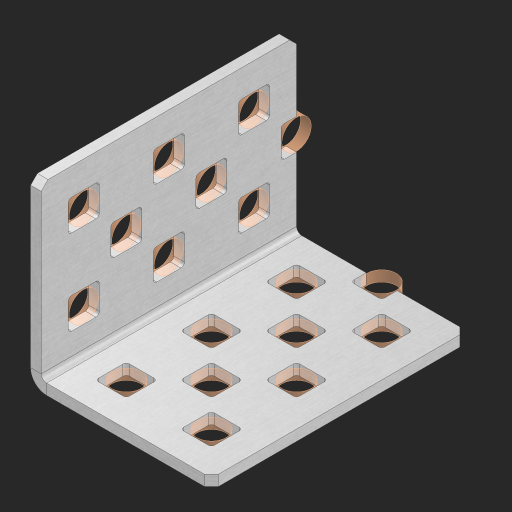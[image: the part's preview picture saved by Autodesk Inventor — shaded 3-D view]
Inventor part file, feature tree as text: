
AUTODESK INVENTOR PART (.ipt)
format: ipt  version: 2023 (Build 270158000, 158)  size: 625,152 bytes
history: native  units: in
note: dims shown in document units (in); Inventor stores cm internally (conversion verified against a paired STEP export)
features: other x24, extrude x16, sheet_metal_op x8, sketch x7, pattern_linear x2, mirror x1, chamfer x1
ambient origin geometry x8: Origin, YZ Plane, XZ Plane, XY Plane, X Axis, Y Axis, Z Axis, Center Point
bodies: Solid1 (feature_tree), Body (feature_tree)
feature tree (59):
  sheet_metal_op  "Flanges"
  sheet_metal_op  "Body Pattern"
  pattern_linear  "Center Pattern"  Spacing1=1.0in  [1 undecoded]
  other  "Arc Length"
  pattern_linear  "Notch Pattern"  Spacing1=0.25in  [1 undecoded]
  other  "Diagonal Plane"
  mirror  "Everything Mirrored"
  chamfer  "End Chamfer"
  sketch  "Sketch1"  dims[d0=1.0in]
  other  "Plate1"
  sketch  "Sketch2"  dims[d1=1.5in]
  other  "Plate2"
  sheet_metal_op  "Bend1"
  sheet_metal_op  "Corner1"
  sketch  "Sketch8"  dims[d2=0.0625in]
  sketch  "Sketch9"  dims[d3=0.0625in]
  other  "Srf91"
  sheet_metal_op  "Body Pattern Sketch"
  other  "Srf92"
  sketch  "Sketch13"  dims[d4=0.0312in]
  sketch  "Sketch15"  dims[d5=0.125in]
  sketch  "Sketch16"  dims[d6=0.0625in d7=1.0in d8=90.0deg d9=0.0312in d10=0.25in d11=0.0625in d12=0.0625in d49=0.182in d50=0.02in d52=0.25in d53=0.0625in d54=0.0in d55=0.172in d56=1.0in d57=0.0in d60=1.1811in d62=0.5in d63=0.7874in d65=0.5in d85=0.1473in d86=0.1782in d89=0.0625in d90=0.0in d91=0.04in d92=0.0491in d95=2.5in d96=0.04in d97=0.25in d98=45.0deg d99=0.25in d106=0.182in d107=0.02in d108=0.5in d110=0.0625in d111=0.0in d112=0.172in d113=0.5in d114=0.0in d117=0.5in d123=0.25in d125=0.25in d126=0.0491in d127=0.1473in d128=0.08in d129=0.04in d130=2.5in]
  other  "Srf786"
  other  "Srf856"
  other  "Srf857"
  other  "Srf858"
  other  "Srf859"
  other  "Srf889"
  other  "Srf890"
  other  "Srf1275"
  other  "Srf1276"
  other  "Srf1278"
  other  "Srf1279"
  other  "Srf1280"
  other  "Srf1281"
  other  "Srf1277"
  other  "Srf1285"
  other  "Srf1286"
  sheet_metal_op  "Body Stamp"
  sheet_metal_op  "Body Circle"
  other  "Center Stamp"
  other  "Center Circle"
  sheet_metal_op  "Notch"
  extrude  "ExtrusionSrf92"  Depth=0.0625in
  extrude  "ExtrusionSrf856"  Depth=0.0625in
  extrude  "ExtrusionSrf857"  Depth=0.182in
  extrude  "ExtrusionSrf858"  Depth=0.02in
  extrude  "ExtrusionSrf859"  Depth=0.25in
  extrude  "ExtrusionSrf889"  Depth=0.0625in
  extrude  "ExtrusionSrf890"  TaperAngle=0.0deg  [1 undecoded]
  extrude  "ExtrusionSrf1275"  Depth=0.25in
  extrude  "ExtrusionSrf1276"  Depth=1.0in TaperAngle=0.0deg
  extrude  "ExtrusionSrf1277"  Depth=0.25in
  extrude  "ExtrusionSrf1278"  Depth=0.5in
  extrude  "ExtrusionSrf1279"  Depth=0.25in
  extrude  "ExtrusionSrf1280"  Depth=0.25in
  extrude  "ExtrusionSrf1345"  Depth=0.0625in
  extrude  "ExtrusionSrf1346"  Depth=0.25in TaperAngle=0.0deg
  extrude  "ExtrusionSrf1347"  Depth=0.25in
note: 3 required parameter values undecoded (feature->parameter linkage not recoverable at this tier; creation-order binding heuristic only, values carry confidence <= 0.55)
